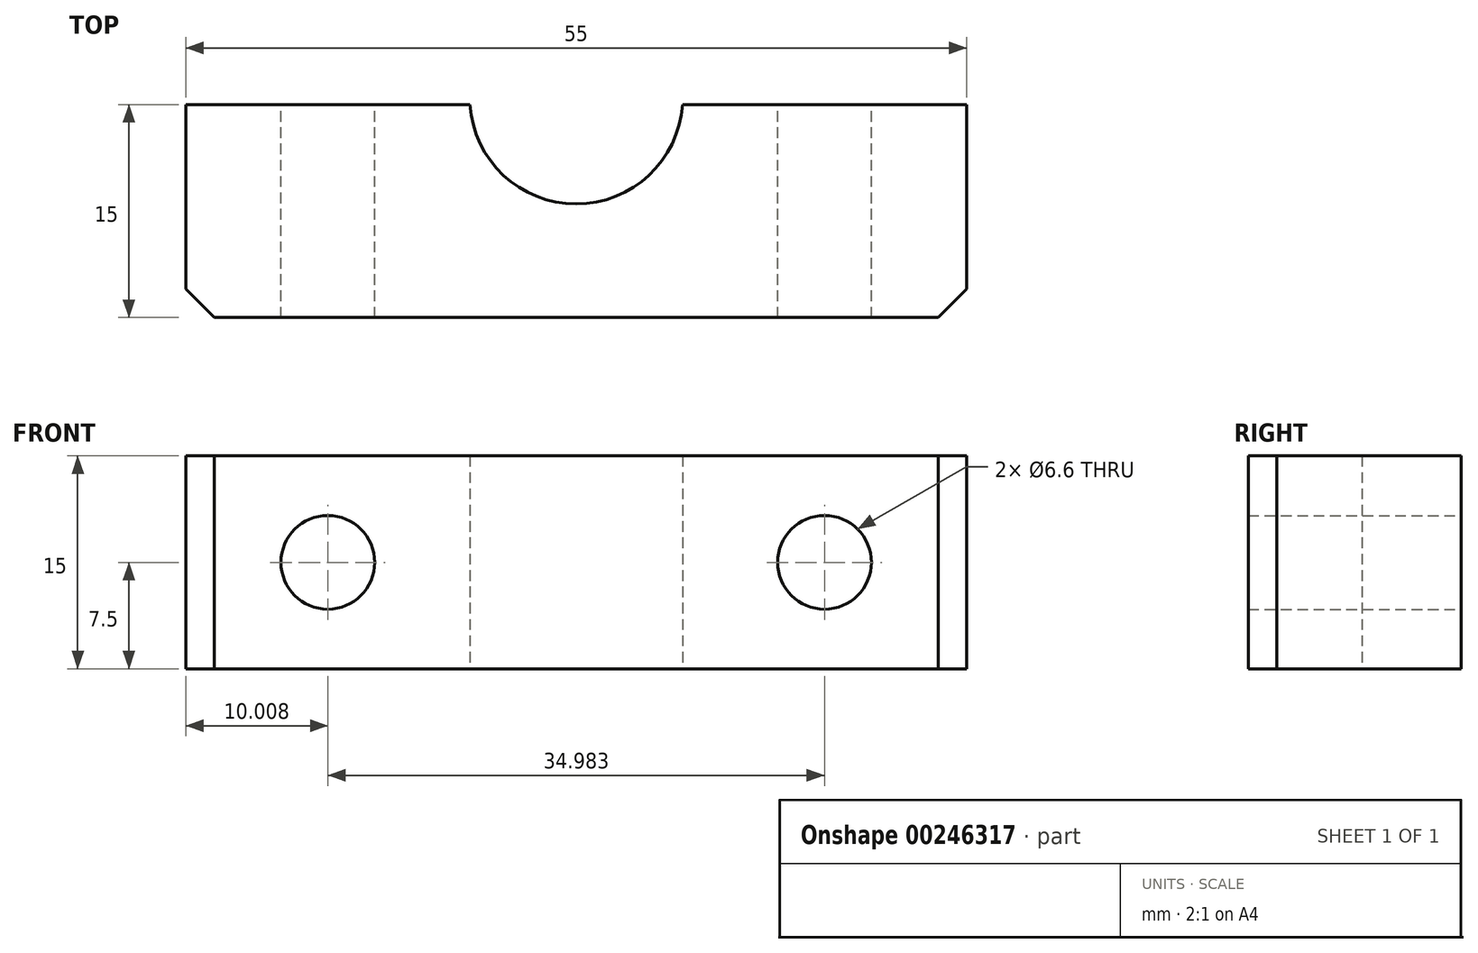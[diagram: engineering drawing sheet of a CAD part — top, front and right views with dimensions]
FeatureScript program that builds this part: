
annotation { "Feature Type Name" : "Feature", "Feature Type Description" : "" }
export const myFeature = defineFeature(function(context is Context, id is Id, definition is map)
    precondition{}
    {
        {
            var Q0;
            Q0=qCreatedBy(makeId("Top.planeOp"),FACE);
            var sketch = newSketch(context, id + "F0", { "sketchPlane" : qUnion([Q0])});
            skArc(sketch, "E0", {"start": v(-7.48, -0.5) * mm, "mid": v(0, -7.5) * mm, "end": v(7.48, -0.5) * mm});
            skLineSegment(sketch, "E1.bottom", {"start": v(-27.5, -0.5) * mm, "end": v(-7.48, -0.5) * mm});
            skLineSegment(sketch, "E1.top", {"start": v(-27.5, -15.5) * mm, "end": v(27.5, -15.5) * mm});
            skLineSegment(sketch, "E1.left", {"start": v(-27.5, -0.5) * mm, "end": v(-27.5, -15.5) * mm});
            skLineSegment(sketch, "E1.right", {"start": v(27.5, -0.5) * mm, "end": v(27.5, -15.5) * mm});
            skLineSegment(sketch, "E2.trimOffspring", {"start": v(7.48, -0.5) * mm, "end": v(27.5, -0.5) * mm});
            skSolve(sketch);
        }
        {
            var Q0;
            Q0 = qSketchRegion(id + "F0", true);
            extrude(context, id + "F1", {"entities" : qUnion([Q0]), "depth" : 15 * mm});
        }
        {
            var Q0;
            Q0=makeQuery(id+"F1.opExtrude","SWEPT_FACE",FACE,{"disambiguationData":[OSD([sQuery(id+"F0.wireOp",EDGE,"E2.trimOffspring")])]});
            var sketch = newSketch(context, id + "F2", { "sketchPlane" : qUnion([Q0])});
            skPoint(sketch, "E3.0", {"position": v(7.48, 7.5) * mm});
            skPoint(sketch, "E4.0", {"position": v(17.5, 0) * mm});
            skPoint(sketch, "E5.0", {"position": v(-17.5, 0) * mm});
            skPoint(sketch, "E6.0", {"position": v(-27.5, 7.5) * mm});
            skPoint(sketch, "E7", {"position": v(17.5, 7.5) * mm});
            skPoint(sketch, "E8", {"position": v(-17.5, 7.5) * mm});
            skPoint(sketch, "E8.positionSnap0", {"position": v(-17.5, 15) * mm});
            skSolve(sketch);
        }
        {
            var Q0;
            Q0=sQuery(id+"F2.wireOp",VERTEX,"E7");
            var Q1;
            Q1=sQuery(id+"F2.wireOp",VERTEX,"E8");
            var Q2;
            Q2=makeQuery(id+"F1.opExtrude","SWEPT_BODY",BODY,{"disambiguationData":[OSD([sQuery(id+"F0.wireOp",EDGE,"E0"),sQuery(id+"F0.wireOp",EDGE,"E1.bottom"),sQuery(id+"F0.wireOp",EDGE,"E1.top"),sQuery(id+"F0.wireOp",EDGE,"E1.left"),sQuery(id+"F0.wireOp",EDGE,"E1.right"),sQuery(id+"F0.wireOp",EDGE,"E2.trimOffspring")])]});
            hole(context, id + "F3", {"style" : HoleStyle.SIMPLE, "endStyle" : HoleEndStyle.THROUGH, "holeDiameter" : 6.6 * mm, "tappedDepth" : 12 * mm, "tapClearance" : 3, "locations" : qUnion([Q0, Q1]), "scope" : qUnion([Q2])});
        }
        {
            var Q0;
            Q0=makeQuery(id+"F1.opExtrude","SWEPT_EDGE",EDGE,{"disambiguationData":[OSD([sQuery(id+"F0.wireOp",EDGE,"E1.top"),sQuery(id+"F0.wireOp",EDGE,"E1.left")])]});
            var Q1;
            Q1=makeQuery(id+"F1.opExtrude","SWEPT_EDGE",EDGE,{"disambiguationData":[OSD([sQuery(id+"F0.wireOp",EDGE,"E1.top"),sQuery(id+"F0.wireOp",EDGE,"E1.right")])]});
            chamfer(context, id + "F4", {"entities" : qUnion([Q0, Q1]), "chamferType" : ChamferType.OFFSET_ANGLE, "width" : 2 * mm, "oppositeDirection" : false, "angle" : 45 * degree, "tangentPropagation" : true});
        }
    });
